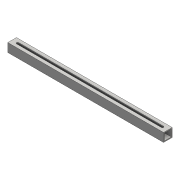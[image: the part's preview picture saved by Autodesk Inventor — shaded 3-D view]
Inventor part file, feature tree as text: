
AUTODESK INVENTOR PART (.ipt)
format: ipt  version: 2016 (Build 200138000, 138)  size: 96,768 bytes
history: native  units: mm
features: extrude x2, sketch x2
ambient origin geometry x8: Origin, YZ Plane, XZ Plane, XY Plane, X Axis, Y Axis, Z Axis, Center Point
bodies: Solid1 (feature_tree)
feature tree (4):
  extrude  "Extrusion1"  Depth=25.4mm
  extrude  "Extrusion2"  Depth=457.2mm TaperAngle=0.0deg
  sketch  "Sketch1"  dims[d0=2.54mm d1=25.4mm]
  sketch  "Sketch2"  dims[d2=25.4mm d3=457.2mm d4=0.0mm d5=6.35mm d6=12.7mm d7=12.7mm d8=9.525mm d9=3.175mm d10=457.2mm d11=0.0mm]
